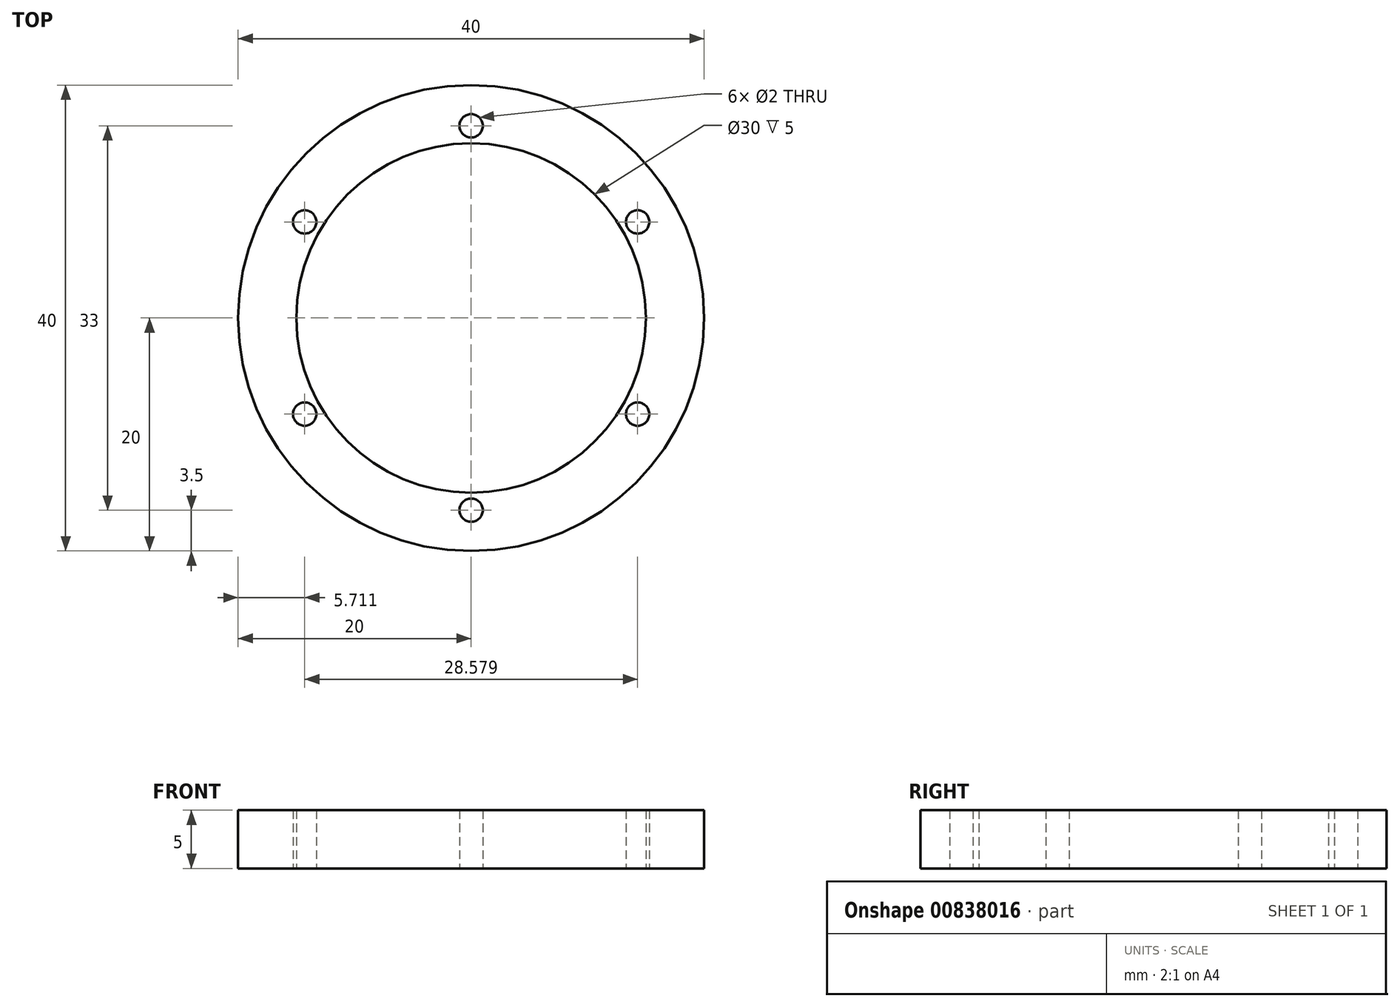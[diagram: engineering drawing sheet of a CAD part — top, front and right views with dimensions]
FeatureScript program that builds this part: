
annotation { "Feature Type Name" : "Feature", "Feature Type Description" : "" }
export const myFeature = defineFeature(function(context is Context, id is Id, definition is map)
    precondition{}
    {
        {
            var Q0;
            Q0=qCreatedBy(makeId("Top.planeOp"),FACE);
            var sketch = newSketch(context, id + "F0", { "sketchPlane" : qUnion([Q0])});
            skCircle(sketch, "E0", {"center": v(0, 0) * mm, "radius": 16.5 * mm});
            skCircle(sketch, "E1", {"center": v(0, 0) * mm, "radius": 15 * mm});
            skCircle(sketch, "E2", {"center": v(0, 0) * mm, "radius": 20 * mm});
            skCircle(sketch, "E3", {"center": v(0, 16.5) * mm, "radius": 1 * mm});
            skCircle(sketch, "E4.1.0", {"center": v(-14.29, 8.25) * mm, "radius": 1 * mm});
            skCircle(sketch, "E4.2.0", {"center": v(-14.29, -8.25) * mm, "radius": 1 * mm});
            skCircle(sketch, "E4.3.0", {"center": v(0, -16.5) * mm, "radius": 1 * mm});
            skCircle(sketch, "E4.4.0", {"center": v(14.29, -8.25) * mm, "radius": 1 * mm});
            skCircle(sketch, "E4.5.0", {"center": v(14.29, 8.25) * mm, "radius": 1 * mm});
            skSolve(sketch);
        }
        {
            var Q0;
            Q0=makeQuery(id+"F0.imprint","IMPRINT",FACE,{"disambiguationData":[TD([[makeQuery(id+"F0.imprint","IMPRINT",EDGE,{"derivedFrom":sQuery(id+"F0.wireOp",EDGE,"E2")}),1.0]])]});
            var Q1;
            Q1=makeQuery(id+"F0.imprint","IMPRINT",FACE,{"disambiguationData":[TD([[makeQuery(id+"F0.imprint","IMPRINT",EDGE,{"derivedFrom":sQuery(id+"F0.wireOp",EDGE,"E1")}),-1.0]])]});
            extrude(context, id + "F1", {"entities" : qUnion([Q0, Q1]), "depth" : 5 * mm, "offsetDistance" : 25 * mm});
        }
    });
